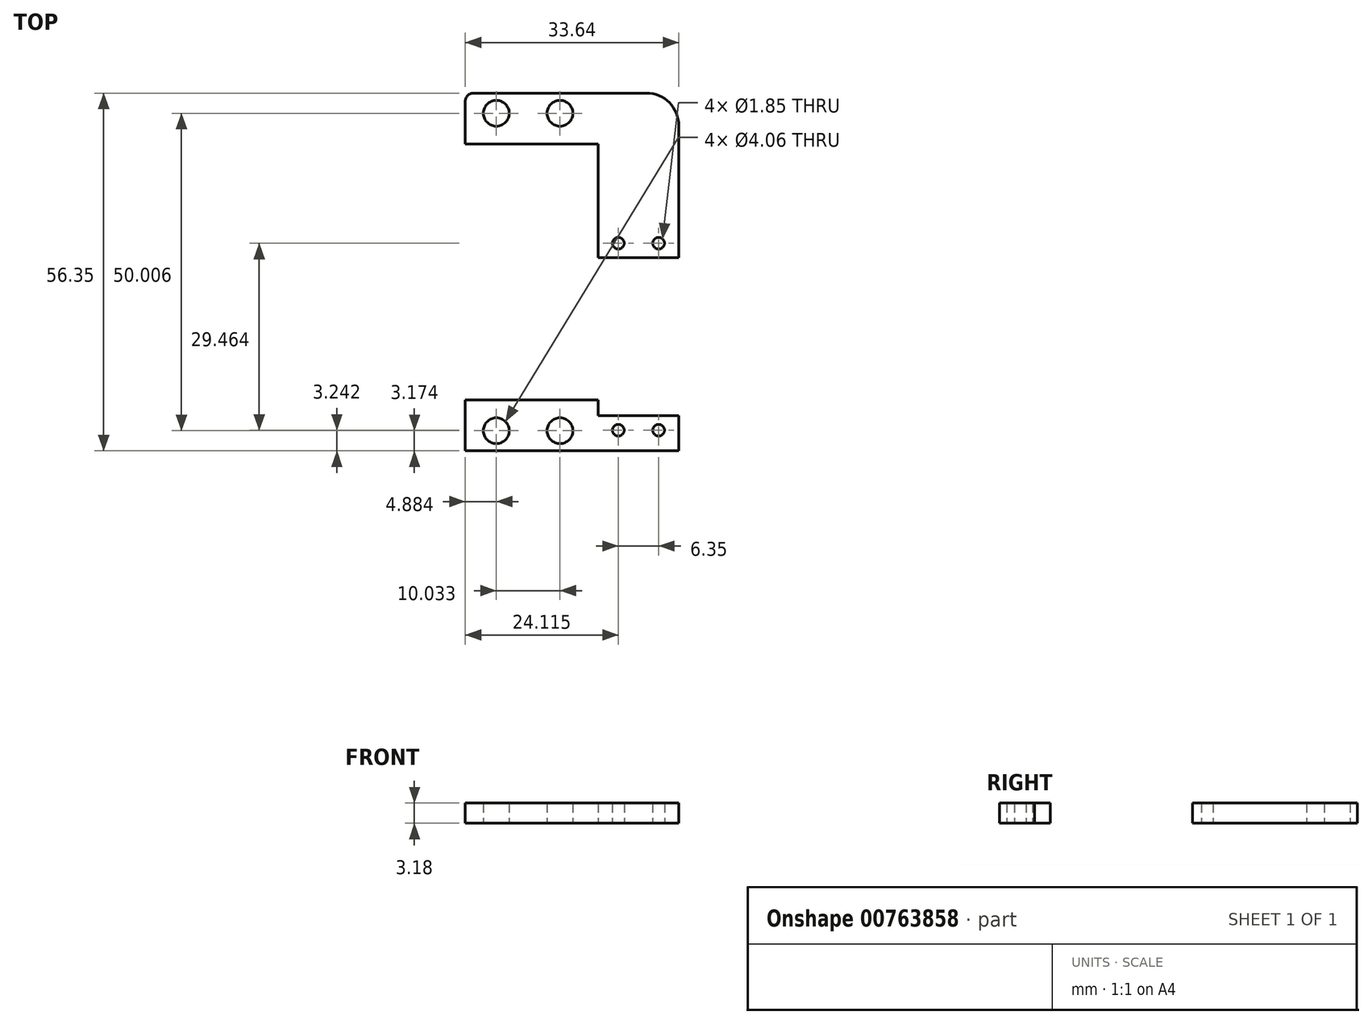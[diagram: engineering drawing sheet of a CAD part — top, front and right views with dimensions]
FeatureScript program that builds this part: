
annotation { "Feature Type Name" : "Feature", "Feature Type Description" : "" }
export const myFeature = defineFeature(function(context is Context, id is Id, definition is map)
    precondition{}
    {
        {
            var Q0;
            Q0=qCreatedBy(makeId("Top.planeOp"),FACE);
            var sketch = newSketch(context, id + "F0", { "sketchPlane" : qUnion([Q0])});
            skCircle(sketch, "E0", {"center": v(-5.02, 0) * mm, "radius": 2.03 * mm});
            skCircle(sketch, "E1", {"center": v(5.02, 0) * mm, "radius": 2.03 * mm});
            skLineSegment(sketch, "E2", {"start": v(-5.02, 0) * mm, "end": v(5.02, 0) * mm, "construction": true});
            skLineSegment(sketch, "E3.bottom", {"start": v(11.04, -4.83) * mm, "end": v(-9.9, -4.83) * mm});
            skLineSegment(sketch, "E3.top", {"start": v(11.04, 3.18) * mm, "end": v(-8.63, 3.17) * mm});
            skLineSegment(sketch, "E3.left", {"start": v(11.04, -4.83) * mm, "end": v(11.04, 3.18) * mm});
            skLineSegment(sketch, "E3.right", {"start": v(-9.9, -4.83) * mm, "end": v(-9.9, 1.9) * mm});
            skPoint(sketch, "E3.middle", {"position": v(0, 0) * mm});
            skLineSegment(sketch, "E4.bottom", {"start": v(11.04, 3.18) * mm, "end": v(18.66, 3.18) * mm});
            skLineSegment(sketch, "E4.top", {"start": v(11.04, -22.76) * mm, "end": v(23.74, -22.76) * mm});
            skLineSegment(sketch, "E4.left", {"start": v(11.04, 3.18) * mm, "end": v(11.04, -22.76) * mm});
            skLineSegment(sketch, "E4.right", {"start": v(23.74, -1.9) * mm, "end": v(23.74, -22.76) * mm});
            skLineSegment(sketch, "E5", {"start": v(0, 3.18) * mm, "end": v(0, -4.83) * mm, "construction": true});
            skCircle(sketch, "E6", {"center": v(14.21, -20.47) * mm, "radius": 0.93 * mm});
            skCircle(sketch, "E7", {"center": v(20.56, -20.47) * mm, "radius": 0.93 * mm});
            skLineSegment(sketch, "E8", {"start": v(14.21, -20.47) * mm, "end": v(20.56, -20.47) * mm, "construction": true});
            skLineSegment(sketch, "E9", {"start": v(17.39, -20.47) * mm, "end": v(17.39, -16.5) * mm, "construction": true});
            skPoint(sketch, "E10.visualSharp", {"position": v(23.74, 3.18) * mm});
            skArc(sketch, "E10.filletArc", {"start": v(23.74, -1.9) * mm, "mid": v(22.25, 1.69) * mm, "end": v(18.66, 3.18) * mm});
            skPoint(sketch, "E11.visualSharp", {"position": v(-9.9, 3.17) * mm});
            skArc(sketch, "E11.filletArc", {"start": v(-8.63, 3.17) * mm, "mid": v(-9.53, 2.8) * mm, "end": v(-9.9, 1.9) * mm});
            skLineSegment(sketch, "E12.bottom", {"start": v(-9.9, -45.18) * mm, "end": v(11.04, -45.18) * mm});
            skLineSegment(sketch, "E12.top", {"start": v(-9.9, -53.18) * mm, "end": v(11.04, -53.18) * mm});
            skLineSegment(sketch, "E12.left", {"start": v(-9.9, -45.18) * mm, "end": v(-9.9, -53.18) * mm});
            skLineSegment(sketch, "E12.right", {"start": v(11.04, -45.18) * mm, "end": v(11.04, -53.18) * mm});
            skCircle(sketch, "E13", {"center": v(-5.02, -50) * mm, "radius": 2.03 * mm});
            skCircle(sketch, "E14", {"center": v(5.02, -50) * mm, "radius": 2.03 * mm});
            skLineSegment(sketch, "E15", {"start": v(-5.02, -50) * mm, "end": v(5.02, -50) * mm, "construction": true});
            skLineSegment(sketch, "E16", {"start": v(0, -50) * mm, "end": v(0, -45.18) * mm, "construction": true});
            skPoint(sketch, "E16.startSnap0", {"position": v(0, -50) * mm});
            skCircle(sketch, "E17", {"center": v(14.21, -49.94) * mm, "radius": 0.93 * mm});
            skCircle(sketch, "E18", {"center": v(20.56, -49.94) * mm, "radius": 0.93 * mm});
            skLineSegment(sketch, "E19", {"start": v(14.21, -49.94) * mm, "end": v(20.56, -49.94) * mm, "construction": true});
            skLineSegment(sketch, "E20", {"start": v(17.39, -49.94) * mm, "end": v(17.39, -50.77) * mm, "construction": true});
            skLineSegment(sketch, "E21.bottom", {"start": v(11.04, -53.18) * mm, "end": v(23.74, -53.18) * mm});
            skLineSegment(sketch, "E21.top", {"start": v(11.04, -47.65) * mm, "end": v(23.74, -47.65) * mm});
            skLineSegment(sketch, "E21.left", {"start": v(11.04, -53.18) * mm, "end": v(11.04, -47.65) * mm});
            skLineSegment(sketch, "E21.right", {"start": v(23.74, -53.18) * mm, "end": v(23.74, -47.65) * mm});
            skSolve(sketch);
        }
        {
            var Q0;
            Q0 = qSketchRegion(id + "F0", true);
            extrude(context, id + "F1", {"entities" : qUnion([Q0]), "depth" : 3.17 * mm, "offsetDistance" : 25.4 * mm});
        }
    });
